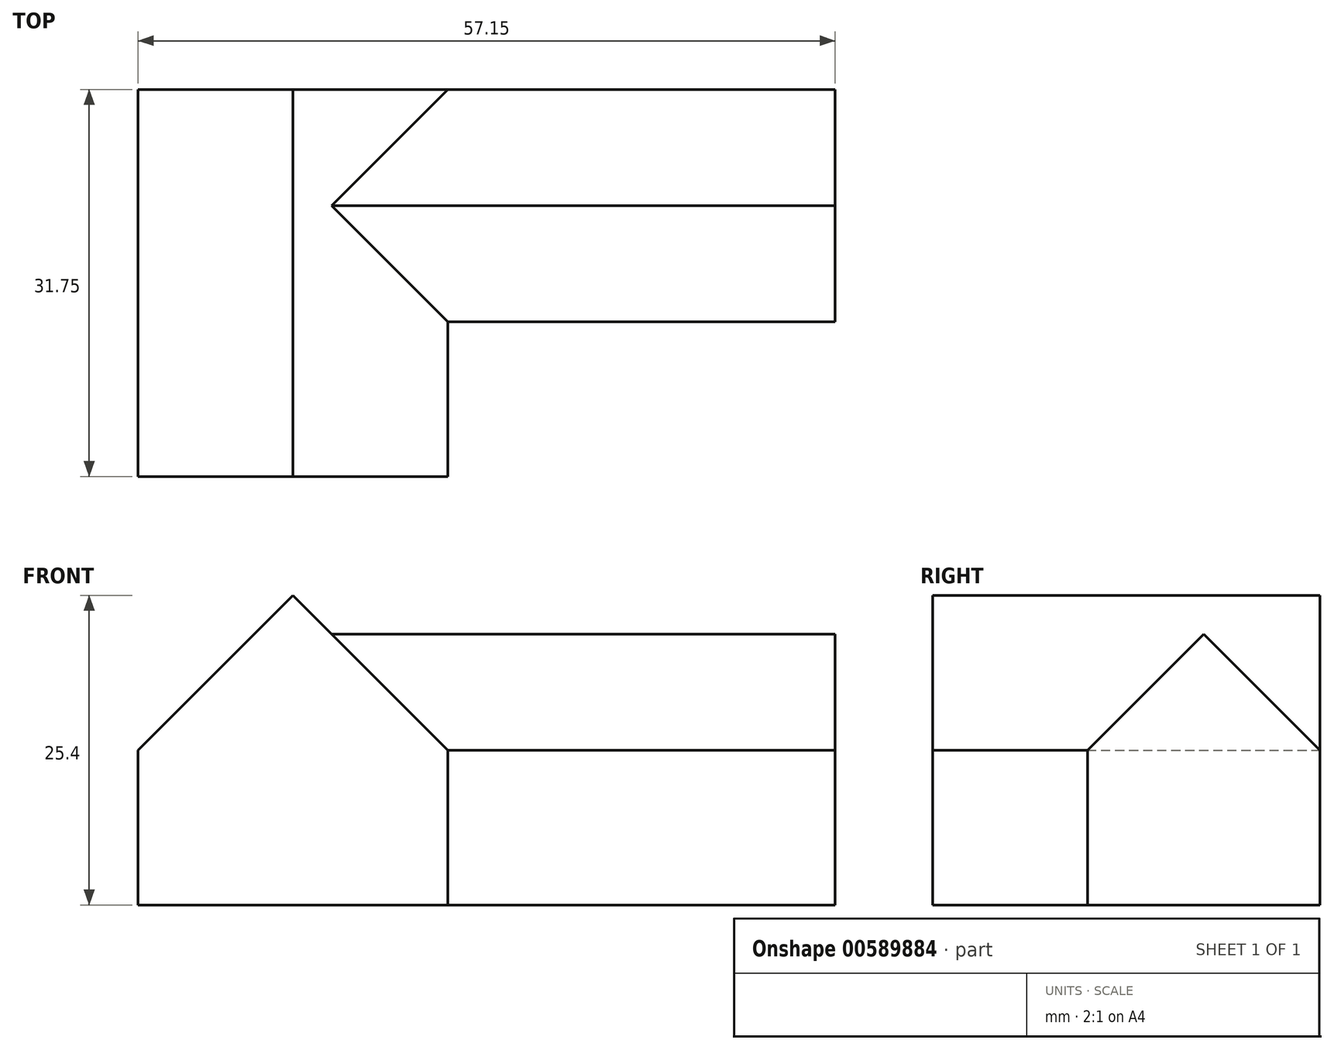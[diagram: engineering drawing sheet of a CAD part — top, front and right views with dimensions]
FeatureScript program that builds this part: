
annotation { "Feature Type Name" : "Feature", "Feature Type Description" : "" }
export const myFeature = defineFeature(function(context is Context, id is Id, definition is map)
    precondition{}
    {
        {
            var Q0;
            Q0=qCreatedBy(makeId("Top.planeOp"),FACE);
            var sketch = newSketch(context, id + "F0", { "sketchPlane" : qUnion([Q0])});
            skLineSegment(sketch, "E0.bottom", {"start": v(0, 0) * mm, "end": v(25.4, 0) * mm});
            skLineSegment(sketch, "E0.top", {"start": v(0, 31.75) * mm, "end": v(57.15, 31.75) * mm});
            skLineSegment(sketch, "E0.left", {"start": v(0, 0) * mm, "end": v(0, 31.75) * mm});
            skLineSegment(sketch, "E1", {"start": v(25.4, 0) * mm, "end": v(25.4, 12.7) * mm});
            skLineSegment(sketch, "E2", {"start": v(25.4, 12.7) * mm, "end": v(57.15, 12.7) * mm});
            skLineSegment(sketch, "E3", {"start": v(57.15, 12.7) * mm, "end": v(57.15, 31.75) * mm});
            skPoint(sketch, "E4.end.orphan", {"position": v(50.8, 0) * mm});
            skLineSegment(sketch, "E5", {"start": v(25.4, 12.7) * mm, "end": v(25.4, 31.75) * mm});
            skPoint(sketch, "E5.endSnap0", {"position": v(28.58, 31.75) * mm});
            skSolve(sketch);
        }
        {
            var Q0;
            Q0=makeQuery(id+"F0.imprint","IMPRINT",FACE,{"disambiguationData":[TD([[makeQuery(id+"F0.imprint","IMPRINT",EDGE,{"derivedFrom":sQuery(id+"F0.wireOp",EDGE,"E0.bottom")}),1.0]])]});
            extrude(context, id + "F1", {"entities" : qUnion([Q0]), "depth" : 25.4 * mm, "offsetDistance" : 25.4 * mm});
        }
        {
            var Q0;
            Q0 = qSketchRegion(id + "F0", true);
            extrude(context, id + "F2", {"entities" : qUnion([Q0]), "operationType" : NewBodyOperationType.ADD, "depth" : 22.22 * mm, "offsetDistance" : 25.4 * mm});
        }
        {
            var Q0;
            Q0=makeQuery(id+"F1.opExtrude","CAP_EDGE",EDGE,{"disambiguationData":[OSD([sQuery(id+"F0.wireOp",EDGE,"E1"),sQuery(id+"F0.wireOp",EDGE,"E5")])],"isStart":false});
            var Q1;
            Q1=makeQuery(id+"F1.opExtrude","CAP_EDGE",EDGE,{"disambiguationData":[OSD([sQuery(id+"F0.wireOp",EDGE,"E0.left")])],"isStart":false});
            chamfer(context, id + "F3", {"entities" : qUnion([Q0, Q1]), "width" : 12.7 * mm, "tangentPropagation" : true});
        }
        {
            var Q0;
            Q0=makeQuery(id+"F2.opExtrude","CAP_EDGE",EDGE,{"disambiguationData":[OSD([sQuery(id+"F0.wireOp",EDGE,"E2")])],"isStart":false});
            var Q1;
            Q1=makeQuery(id+"F2.opExtrude","CAP_EDGE",EDGE,{"disambiguationData":[OSD([sQuery(id+"F0.wireOp",EDGE,"E0.top")])],"isStart":false});
            chamfer(context, id + "F4", {"entities" : qUnion([Q0, Q1]), "width" : 9.52 * mm, "tangentPropagation" : true});
        }
    });
